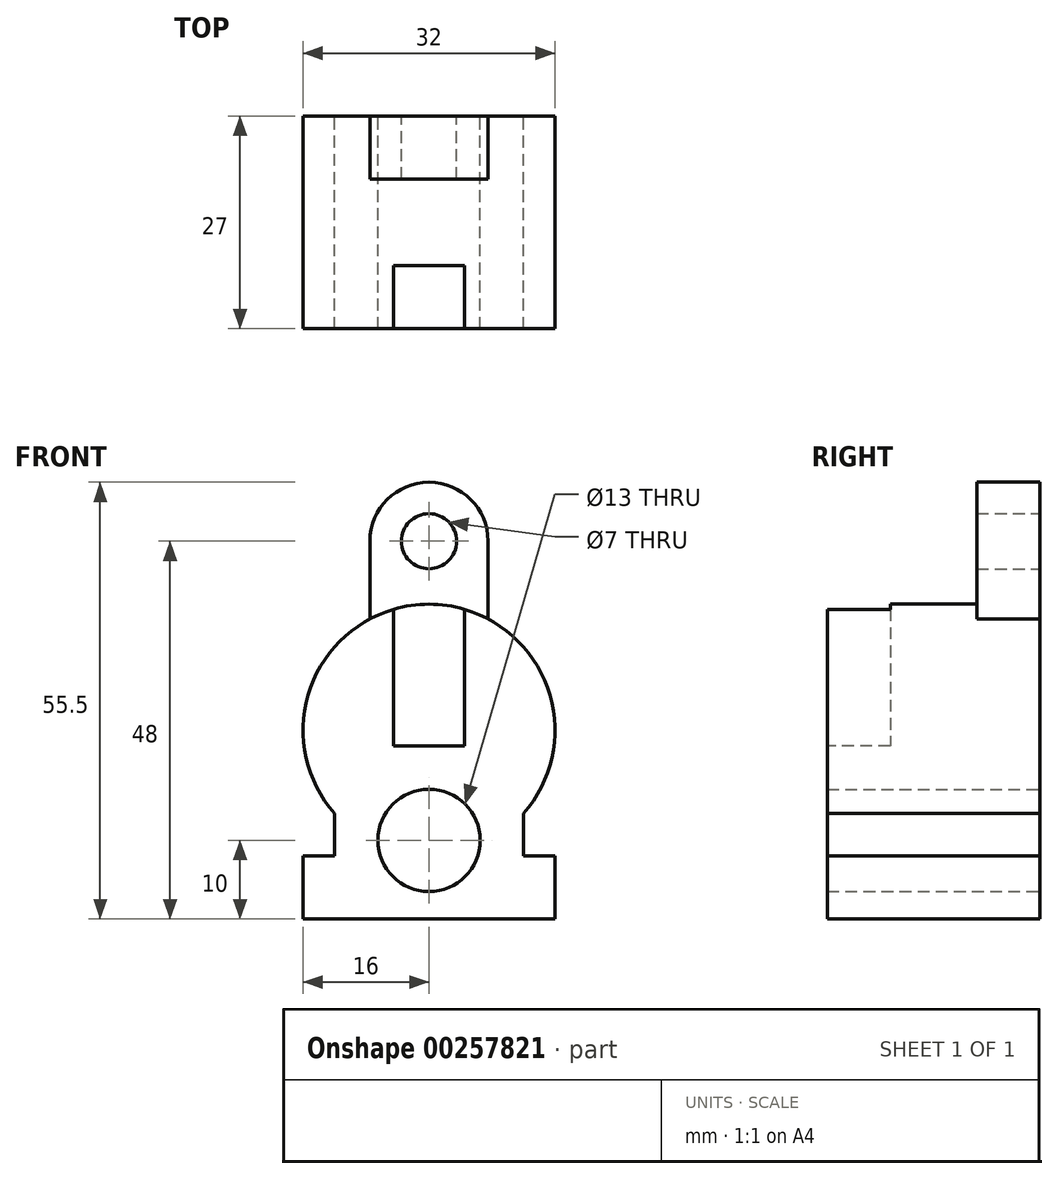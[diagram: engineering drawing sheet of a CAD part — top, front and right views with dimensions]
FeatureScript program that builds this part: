
annotation { "Feature Type Name" : "Feature", "Feature Type Description" : "" }
export const myFeature = defineFeature(function(context is Context, id is Id, definition is map)
    precondition{}
    {
        {
            var Q0;
            Q0=qCreatedBy(makeId("Front.planeOp"),FACE);
            var sketch = newSketch(context, id + "F0", { "sketchPlane" : qUnion([Q0])});
            skLineSegment(sketch, "E0.bottom", {"start": v(-16, 8) * mm, "end": v(16, 8) * mm});
            skLineSegment(sketch, "E0.top", {"start": v(-16, 0) * mm, "end": v(16, 0) * mm});
            skLineSegment(sketch, "E0.left", {"start": v(-16, 8) * mm, "end": v(-16, 0) * mm});
            skLineSegment(sketch, "E0.right", {"start": v(16, 8) * mm, "end": v(16, 0) * mm});
            skLineSegment(sketch, "E1.bottom", {"start": v(-12, 8) * mm, "end": v(12, 8) * mm});
            skLineSegment(sketch, "E1.top", {"start": v(-12, 22) * mm, "end": v(12, 22) * mm});
            skLineSegment(sketch, "E1.left", {"start": v(-12, 8) * mm, "end": v(-12, 22) * mm});
            skLineSegment(sketch, "E1.right", {"start": v(12, 8) * mm, "end": v(12, 22) * mm});
            skCircle(sketch, "E2", {"center": v(0, 24) * mm, "radius": 16 * mm});
            skCircle(sketch, "E3", {"center": v(0, 10) * mm, "radius": 6.5 * mm});
            skCircle(sketch, "E4", {"center": v(0, 48) * mm, "radius": 7.5 * mm});
            skLineSegment(sketch, "E5.bottom", {"start": v(-7.5, 48) * mm, "end": v(7.5, 48) * mm});
            skLineSegment(sketch, "E5.top", {"start": v(-7.5, 38.13) * mm, "end": v(7.5, 38.13) * mm});
            skLineSegment(sketch, "E5.left", {"start": v(-7.5, 48) * mm, "end": v(-7.5, 38.13) * mm});
            skLineSegment(sketch, "E5.right", {"start": v(7.5, 48) * mm, "end": v(7.5, 38.13) * mm});
            skCircle(sketch, "E6", {"center": v(0, 48) * mm, "radius": 3.5 * mm});
            skSolve(sketch);
        }
        {
            var Q0;
            {var subQ5=sQuery(id+"F0.wireOp",EDGE,"E1.top");Q0=makeQuery(id+"F0.imprint","IMPRINT",FACE,{"disambiguationData":[TD([[makeQuery(id+"F0.imprint","IMPRINT",EDGE,{"derivedFrom":subQ5}),1.0]])]});}
            var Q1;
            {var subQ6=sQuery(id+"F0.wireOp",EDGE,"E1.top");Q1=makeQuery(id+"F0.imprint","IMPRINT",FACE,{"disambiguationData":[TD([[makeQuery(id+"F0.imprint","IMPRINT",EDGE,{"derivedFrom":subQ6}),-1.0]])]});}
            var Q2;
            {var subQ0=sQuery(id+"F0.wireOp",EDGE,"E5.top");Q2=makeQuery(id+"F0.imprint","IMPRINT",FACE,{"disambiguationData":[TD([[makeQuery(id+"F0.imprint","IMPRINT",EDGE,{"derivedFrom":subQ0}),1.0]])]});}
            var Q3;
            Q3=makeQuery(id+"F0.imprint","IMPRINT",FACE,{"disambiguationData":[TD([[makeQuery(id+"F0.imprint","IMPRINT",EDGE,{"derivedFrom":sQuery(id+"F0.wireOp",EDGE,"E0.top")}),1.0]])]});
            var Q4;
            {var subQ0=sQuery(id+"F0.wireOp",EDGE,"E1.right");var subQ5=sQuery(id+"F0.wireOp",EDGE,"E2");var subQ6=makeQuery(id+"F0.imprint","INTERSECT",VERTEX,{"derivedFrom":[subQ0,subQ5]});Q4=makeQuery(id+"F0.imprint","IMPRINT",FACE,{"disambiguationData":[TD([[makeQuery(id+"F0.imprint","IMPRINT",EDGE,{"disambiguationData":[TD([[subQ6,1.0]])],"derivedFrom":subQ5}),-1.0]])]});}
            var Q5;
            {var subQ0=sQuery(id+"F0.wireOp",EDGE,"E1.left");var subQ5=sQuery(id+"F0.wireOp",EDGE,"E2");var subQ7=makeQuery(id+"F0.imprint","INTERSECT",VERTEX,{"derivedFrom":[subQ0,subQ5]});Q5=makeQuery(id+"F0.imprint","IMPRINT",FACE,{"disambiguationData":[TD([[makeQuery(id+"F0.imprint","IMPRINT",EDGE,{"disambiguationData":[TD([[subQ7,-1.0]])],"derivedFrom":subQ5}),-1.0]])]});}
            extrude(context, id + "F1", {"entities" : qUnion([Q0, Q1, Q2, Q3, Q4, Q5]), "depth" : 27 * mm});
        }
        {
            var Q0;
            {var subQ0=sQuery(id+"F0.wireOp",EDGE,"E5.bottom");var subQ4=sQuery(id+"F0.wireOp",EDGE,"E6");var subQ5=makeQuery(id+"F0.imprint","INTERSECT",VERTEX,{"disambiguationData":[OD(0.0)],"derivedFrom":[subQ0,subQ4]});Q0=makeQuery(id+"F0.imprint","IMPRINT",FACE,{"disambiguationData":[TD([[makeQuery(id+"F0.imprint","IMPRINT",EDGE,{"disambiguationData":[TD([[subQ5,-1.0]])],"derivedFrom":subQ4}),-1.0]])]});}
            var Q1;
            {var subQ0=sQuery(id+"F0.wireOp",EDGE,"E5.bottom");var subQ4=sQuery(id+"F0.wireOp",EDGE,"E6");var subQ5=makeQuery(id+"F0.imprint","INTERSECT",VERTEX,{"disambiguationData":[OD(0.0)],"derivedFrom":[subQ0,subQ4]});Q1=makeQuery(id+"F0.imprint","IMPRINT",FACE,{"disambiguationData":[TD([[makeQuery(id+"F0.imprint","IMPRINT",EDGE,{"disambiguationData":[TD([[subQ5,1.0]])],"derivedFrom":subQ4}),-1.0]])]});}
            var Q2;
            {var subQ0=sQuery(id+"F0.wireOp",EDGE,"E5.left");Q2=makeQuery(id+"F0.imprint","IMPRINT",FACE,{"disambiguationData":[TD([[makeQuery(id+"F0.imprint","IMPRINT",EDGE,{"derivedFrom":subQ0}),1.0]])]});}
            extrude(context, id + "F2", {"entities" : qUnion([Q0, Q1, Q2]), "operationType" : NewBodyOperationType.ADD, "depth" : 8 * mm});
        }
        {
            var Q0;
            Q0=makeQuery(id+"F1.opExtrude","CAP_FACE",FACE,{"disambiguationData":[OSD([sQuery(id+"F0.wireOp",EDGE,"E0.bottom"),sQuery(id+"F0.wireOp",EDGE,"E0.top"),sQuery(id+"F0.wireOp",EDGE,"E0.left"),sQuery(id+"F0.wireOp",EDGE,"E0.right"),sQuery(id+"F0.wireOp",EDGE,"E1.left"),sQuery(id+"F0.wireOp",EDGE,"E1.right"),sQuery(id+"F0.wireOp",EDGE,"E2"),sQuery(id+"F0.wireOp",EDGE,"E3")])],"isStart":false});
            var sketch = newSketch(context, id + "F3", { "sketchPlane" : qUnion([Q0])});
            skLineSegment(sketch, "E7.top", {"start": v(-4.5, 22) * mm, "end": v(4.5, 22) * mm});
            skLineSegment(sketch, "E7.left", {"start": v(-4.5, 39.35) * mm, "end": v(-4.5, 22) * mm});
            skLineSegment(sketch, "E7.right", {"start": v(4.5, 39.35) * mm, "end": v(4.5, 22) * mm});
            skPoint(sketch, "E8", {"position": v(0, 22) * mm});
            skSolve(sketch);
        }
        {
            var Q0;
            Q0=makeQuery(id+"F3.imprint","IMPRINT",FACE,{"disambiguationData":[TD([[makeQuery(id+"F3.imprint","IMPRINT",EDGE,{"derivedFrom":sQuery(id+"F3.wireOp",EDGE,"E7.top")}),1.0]])]});
            extrude(context, id + "F4", {"entities" : qUnion([Q0]), "operationType" : NewBodyOperationType.REMOVE, "oppositeDirection" : true, "depth" : 8 * mm});
        }
    });
